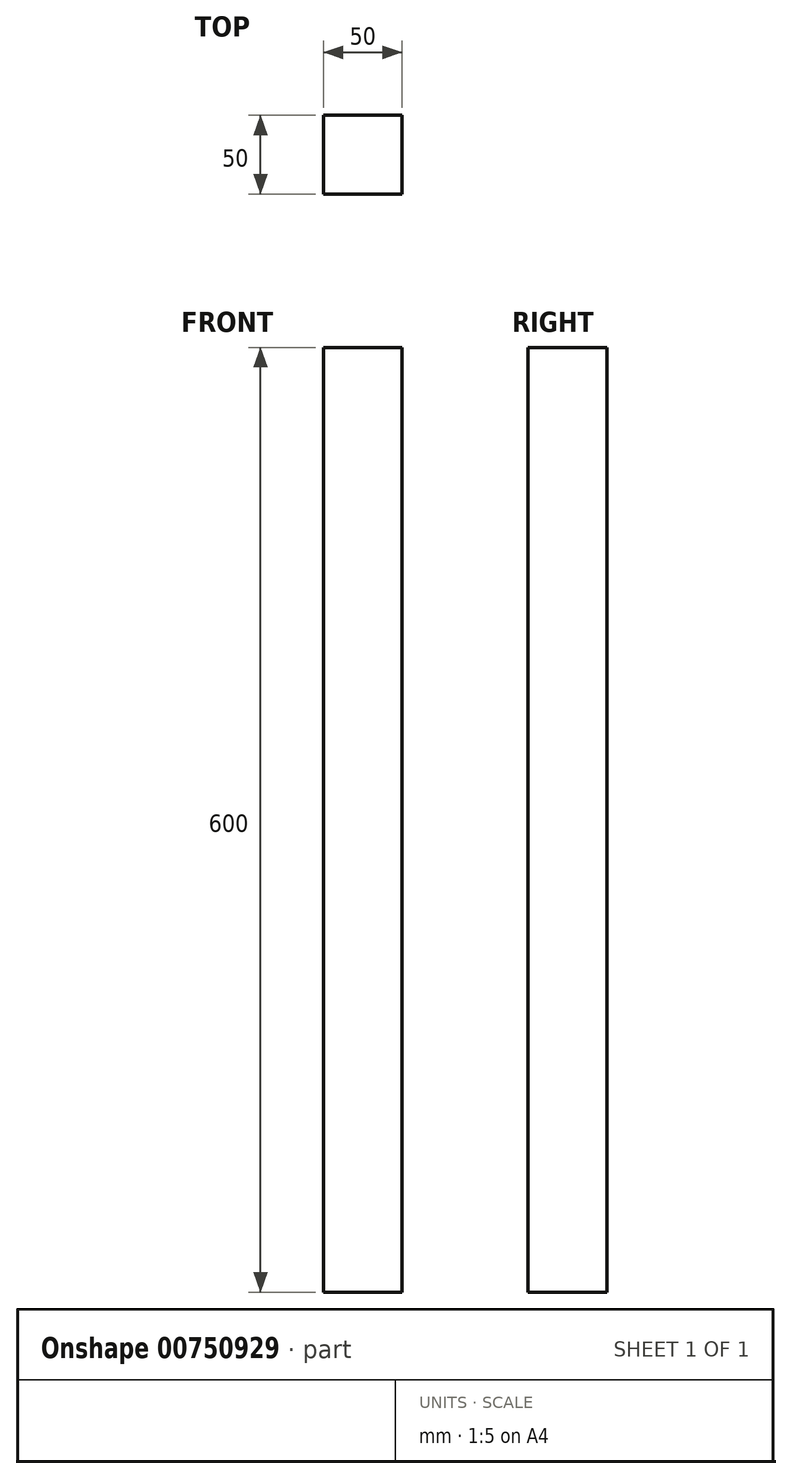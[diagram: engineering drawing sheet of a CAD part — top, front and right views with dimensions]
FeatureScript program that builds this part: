
annotation { "Feature Type Name" : "Feature", "Feature Type Description" : "" }
export const myFeature = defineFeature(function(context is Context, id is Id, definition is map)
    precondition{}
    {
        {
            var Q0;
            Q0=qCreatedBy(makeId("Top.planeOp"),FACE);
            var sketch = newSketch(context, id + "F0", { "sketchPlane" : qUnion([Q0])});
            skLineSegment(sketch, "E0.bottom", {"start": v(25, -25) * mm, "end": v(-25, -25) * mm});
            skLineSegment(sketch, "E0.top", {"start": v(25, 25) * mm, "end": v(-25, 25) * mm});
            skLineSegment(sketch, "E0.left", {"start": v(25, -25) * mm, "end": v(25, 25) * mm});
            skLineSegment(sketch, "E0.right", {"start": v(-25, -25) * mm, "end": v(-25, 25) * mm});
            skPoint(sketch, "E0.middle", {"position": v(0, 0) * mm});
            skSolve(sketch);
        }
        {
            var Q0;
            Q0 = qSketchRegion(id + "F0", true);
            extrude(context, id + "F1", {"entities" : qUnion([Q0]), "depth" : 600 * mm, "offsetDistance" : 25 * mm});
        }
    });
